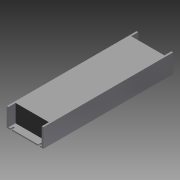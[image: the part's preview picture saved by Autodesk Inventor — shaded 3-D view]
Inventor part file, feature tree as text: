
AUTODESK INVENTOR PART (.ipt)
format: ipt  version: 2013 SP2 (Build 170200200, 200)  size: 152,576 bytes
history: native  units: mm
features: extrude x3, sketch x3, plane x1, mirror x1
ambient origin geometry x8: Origin, YZ Plane, XZ Plane, XY Plane, X Axis, Y Axis, Z Axis, Center Point
bodies: Solid1 (feature_tree)
feature tree (8):
  extrude  "Extrusion1"  Depth=220.0mm
  extrude  "Extrusion2"  Depth=2.8mm
  plane  "Work Plane1"
  mirror  "Mirror1"
  extrude  "Extrusion3"  Depth=2.0mm
  sketch  "Sketch1"  dims[d0=62.0mm d1=220.0mm]
  sketch  "Sketch2"  dims[d2=31.8mm d3=0.0mm d4=2.8mm]
  sketch  "Sketch3"  dims[d5=2.8mm d6=2.0mm d7=12.0mm d8=0.0mm d9=3.0mm d10=3.5mm d11=6.0mm d12=3.5mm d14=3.0mm d15=3.5mm d16=3.0mm d18=3.5mm d19=3.0mm d21=12.0mm d22=0.0mm d23=6.0mm d24=6.0mm d25=6.0mm]
